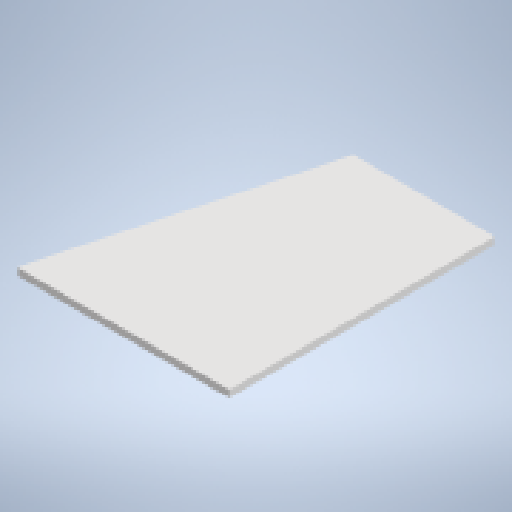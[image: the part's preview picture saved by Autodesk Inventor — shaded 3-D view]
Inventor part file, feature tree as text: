
AUTODESK INVENTOR PART (.ipt)
format: ipt  version: 2025 (Build 290162010, 162A)  size: 152,576 bytes
history: native  units: mm
features: sheet_metal_op x1, chamfer x1, sketch x1, other x1
ambient origin geometry x8: Origin, YZ Plane, XZ Plane, XY Plane, X Axis, Y Axis, Z Axis, Center Point
bodies: Solid1 (feature_tree)
feature tree (4):
  sheet_metal_op  "Face1"
  chamfer  "Corner Round1"
  sketch  "Sketch1"  dims[d2=15.0deg d3=8.0mm d14=2.0mm d29=160.0mm d40=300.0mm d41=15.0deg]
  other  "Plate1"
